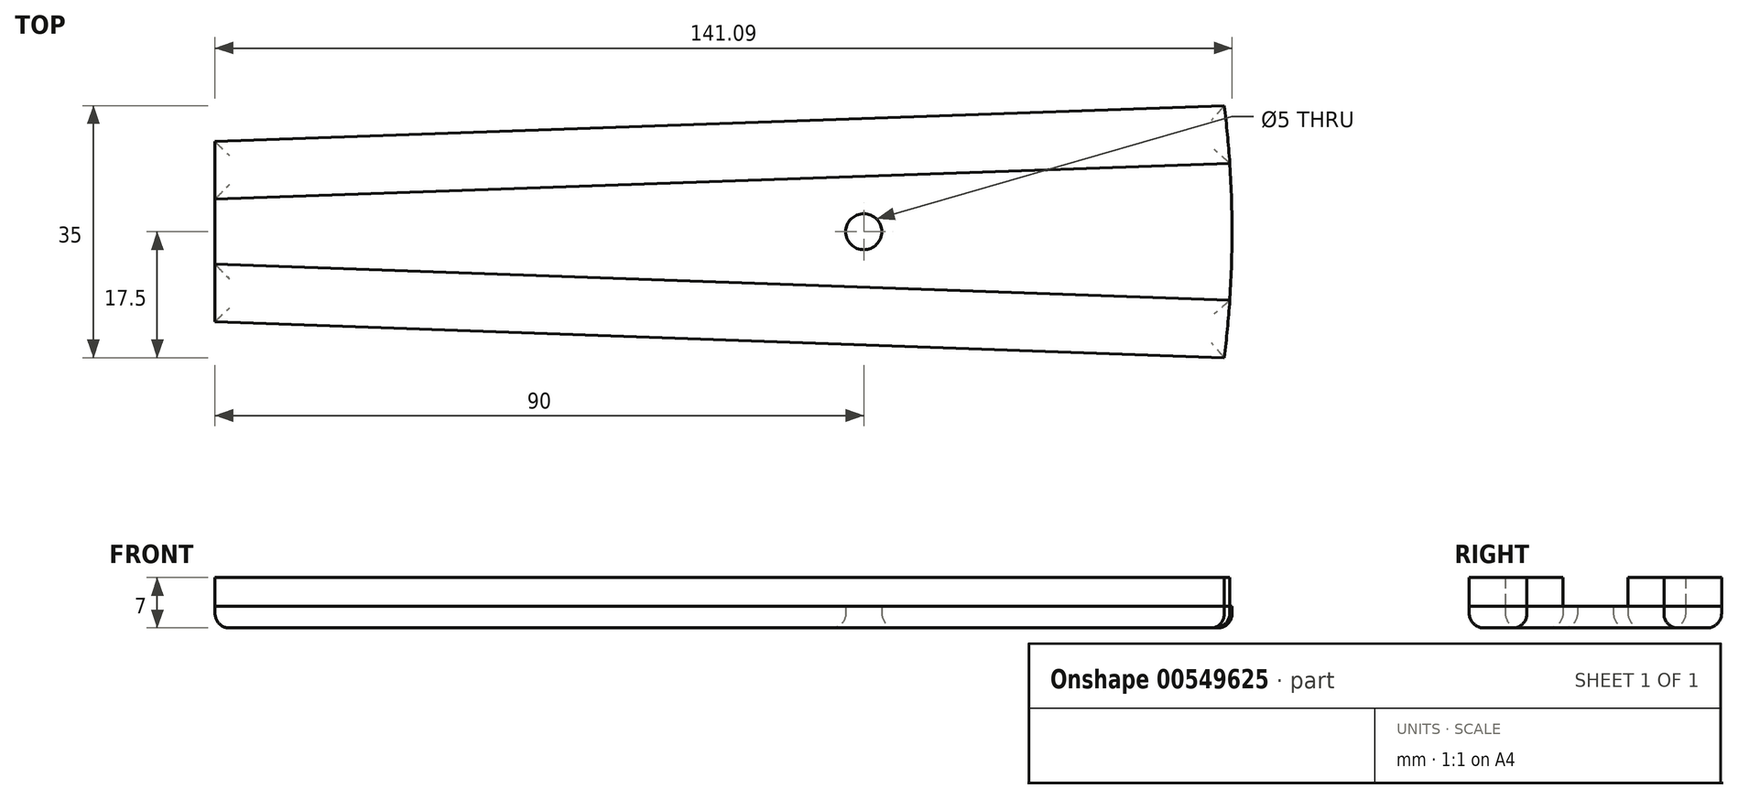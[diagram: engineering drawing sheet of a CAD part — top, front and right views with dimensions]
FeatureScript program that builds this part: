
annotation { "Feature Type Name" : "Feature", "Feature Type Description" : "" }
export const myFeature = defineFeature(function(context is Context, id is Id, definition is map)
    precondition{}
    {
        {
            var Q0;
            Q0=qCreatedBy(makeId("Top.planeOp"),FACE);
            var sketch = newSketch(context, id + "F0", { "sketchPlane" : qUnion([Q0])});
            skPoint(sketch, "E0", {"position": v(-70, 12.5) * mm});
            skPoint(sketch, "E1", {"position": v(-70, -12.5) * mm});
            skPoint(sketch, "E2", {"position": v(70, -17.5) * mm});
            skPoint(sketch, "E3", {"position": v(70, 17.5) * mm});
            skLineSegment(sketch, "E4", {"start": v(-70, 12.5) * mm, "end": v(-70, -12.5) * mm});
            skLineSegment(sketch, "E5", {"start": v(-70, -12.5) * mm, "end": v(70, -17.5) * mm});
            skLineSegment(sketch, "E6", {"start": v(-70, 12.5) * mm, "end": v(70, 17.5) * mm});
            skArc(sketch, "E7", {"start": v(70, -17.5) * mm, "mid": v(71.09, 0) * mm, "end": v(70, 17.5) * mm});
            skPoint(sketch, "E8", {"position": v(-70, -4.5) * mm});
            skPoint(sketch, "E9", {"position": v(-70, 4.5) * mm});
            skPoint(sketch, "E10", {"position": v(70.77, 9.5) * mm});
            skPoint(sketch, "E11", {"position": v(70.77, -9.5) * mm});
            skLineSegment(sketch, "E12", {"start": v(-70, 4.5) * mm, "end": v(70.77, 9.5) * mm});
            skLineSegment(sketch, "E13", {"start": v(-70, -4.5) * mm, "end": v(70.77, -9.5) * mm});
            skCircle(sketch, "E14", {"center": v(20, 0) * mm, "radius": 2.5 * mm});
            skSolve(sketch);
        }
        {
            var Q0;
            {var subQ0=sQuery(id+"F0.wireOp",EDGE,"E6");Q0=makeQuery(id+"F0.imprint","IMPRINT",FACE,{"disambiguationData":[TD([[makeQuery(id+"F0.imprint","IMPRINT",EDGE,{"derivedFrom":subQ0}),-1.0]])]});}
            var Q1;
            {var subQ0=sQuery(id+"F0.wireOp",EDGE,"E5");Q1=makeQuery(id+"F0.imprint","IMPRINT",FACE,{"disambiguationData":[TD([[makeQuery(id+"F0.imprint","IMPRINT",EDGE,{"derivedFrom":subQ0}),1.0]])]});}
            extrude(context, id + "F1", {"entities" : qUnion([Q0, Q1]), "depth" : 7 * mm, "offsetDistance" : 25 * mm});
        }
        {
            var Q0;
            Q0 = qSketchRegion(id + "F0", true);
            extrude(context, id + "F2", {"entities" : qUnion([Q0]), "depth" : 3 * mm, "offsetDistance" : 25 * mm});
        }
        {
            var Q0;
            Q0=makeQuery(id+"F2.opExtrude","CAP_FACE",FACE,{"disambiguationData":[OSD([sQuery(id+"F0.wireOp",EDGE,"E4"),sQuery(id+"F0.wireOp",EDGE,"E5"),sQuery(id+"F0.wireOp",EDGE,"E6"),sQuery(id+"F0.wireOp",EDGE,"E7"),sQuery(id+"F0.wireOp",EDGE,"E14")])],"isStart":true});
            var Q1;
            Q1=makeQuery(id+"F1.opExtrude","CAP_FACE",FACE,{"disambiguationData":[OSD([sQuery(id+"F0.wireOp",EDGE,"E4"),sQuery(id+"F0.wireOp",EDGE,"E6"),sQuery(id+"F0.wireOp",EDGE,"E7"),sQuery(id+"F0.wireOp",EDGE,"E12")])],"isStart":true});
            var Q2;
            Q2=makeQuery(id+"F1.opExtrude","CAP_EDGE",EDGE,{"disambiguationData":[OSD([sQuery(id+"F0.wireOp",EDGE,"E13")])],"isStart":true});
            var Q3;
            Q3=makeQuery(id+"F1.opExtrude","CAP_FACE",FACE,{"disambiguationData":[OSD([sQuery(id+"F0.wireOp",EDGE,"E4"),sQuery(id+"F0.wireOp",EDGE,"E5"),sQuery(id+"F0.wireOp",EDGE,"E7"),sQuery(id+"F0.wireOp",EDGE,"E13")])],"isStart":true});
            fillet(context, id + "F3", {"entities" : qUnion([Q0, Q1, Q2, Q3]), "radius" : 2 * mm, "tangentPropagation" : true, "allowEdgeOverflow" : false});
        }
    });
